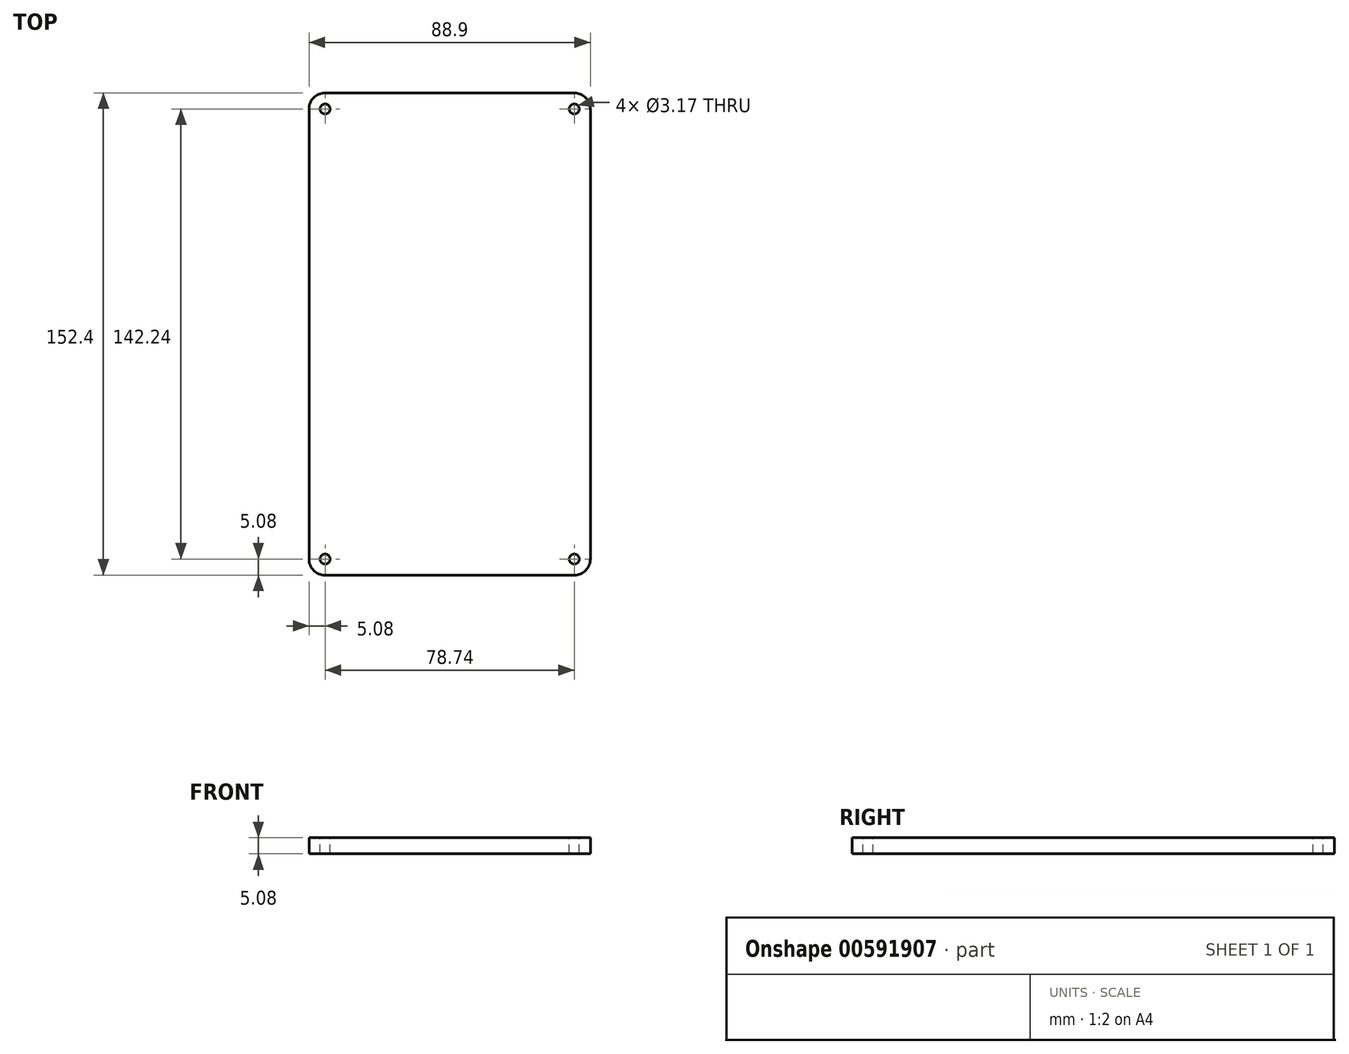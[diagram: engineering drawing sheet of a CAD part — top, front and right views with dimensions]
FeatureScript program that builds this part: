
annotation { "Feature Type Name" : "Feature", "Feature Type Description" : "" }
export const myFeature = defineFeature(function(context is Context, id is Id, definition is map)
    precondition{}
    {
        {
            var Q0;
            Q0=qCreatedBy(makeId("Top.planeOp"),FACE);
            var sketch = newSketch(context, id + "F0", { "sketchPlane" : qUnion([Q0])});
            skLineSegment(sketch, "E0.bottom", {"start": v(0, 0) * mm, "end": v(88.9, 0) * mm});
            skLineSegment(sketch, "E0.top", {"start": v(0, -152.4) * mm, "end": v(88.9, -152.4) * mm});
            skLineSegment(sketch, "E0.left", {"start": v(0, 0) * mm, "end": v(0, -152.4) * mm});
            skLineSegment(sketch, "E0.right", {"start": v(88.9, 0) * mm, "end": v(88.9, -152.4) * mm});
            skSolve(sketch);
        }
        {
            var Q0;
            Q0=makeQuery(id+"F0.imprint","IMPRINT",FACE,{"disambiguationData":[TD([[makeQuery(id+"F0.imprint","IMPRINT",EDGE,{"derivedFrom":sQuery(id+"F0.wireOp",EDGE,"E0.bottom")}),-1.0]])]});
            extrude(context, id + "F1", {"entities" : qUnion([Q0]), "depth" : 5.08 * mm, "offsetDistance" : 25.4 * mm});
        }
        {
            var Q0;
            Q0=makeQuery(id+"F1.opExtrude","CAP_FACE",FACE,{"disambiguationData":[OSD([sQuery(id+"F0.wireOp",EDGE,"E0.bottom"),sQuery(id+"F0.wireOp",EDGE,"E0.top"),sQuery(id+"F0.wireOp",EDGE,"E0.left"),sQuery(id+"F0.wireOp",EDGE,"E0.right")])],"isStart":false});
            var sketch = newSketch(context, id + "F2", { "sketchPlane" : qUnion([Q0])});
            skCircle(sketch, "E1", {"center": v(5.08, -5.08) * mm, "radius": 1.59 * mm});
            skCircle(sketch, "E2", {"center": v(83.82, -5.08) * mm, "radius": 1.59 * mm});
            skCircle(sketch, "E3", {"center": v(5.08, -147.32) * mm, "radius": 1.59 * mm});
            skCircle(sketch, "E4", {"center": v(83.82, -147.32) * mm, "radius": 1.59 * mm});
            skSolve(sketch);
        }
        {
            var Q0;
            Q0=makeQuery(id+"F2.imprint","IMPRINT",FACE,{"disambiguationData":[TD([[makeQuery(id+"F2.imprint","IMPRINT",EDGE,{"derivedFrom":sQuery(id+"F2.wireOp",EDGE,"E1")}),1.0]])]});
            var Q1;
            Q1=makeQuery(id+"F2.imprint","IMPRINT",FACE,{"disambiguationData":[TD([[makeQuery(id+"F2.imprint","IMPRINT",EDGE,{"derivedFrom":sQuery(id+"F2.wireOp",EDGE,"E2")}),1.0]])]});
            var Q2;
            Q2=makeQuery(id+"F2.imprint","IMPRINT",FACE,{"disambiguationData":[TD([[makeQuery(id+"F2.imprint","IMPRINT",EDGE,{"derivedFrom":sQuery(id+"F2.wireOp",EDGE,"E4")}),1.0]])]});
            var Q3;
            Q3=makeQuery(id+"F2.imprint","IMPRINT",FACE,{"disambiguationData":[TD([[makeQuery(id+"F2.imprint","IMPRINT",EDGE,{"derivedFrom":sQuery(id+"F2.wireOp",EDGE,"E3")}),1.0]])]});
            extrude(context, id + "F3", {"entities" : qUnion([Q0, Q1, Q2, Q3]), "operationType" : NewBodyOperationType.REMOVE, "oppositeDirection" : true, "depth" : 25.4 * mm, "offsetDistance" : 25.4 * mm});
        }
        {
            var Q0;
            Q0=makeQuery(id+"F1.opExtrude","SWEPT_EDGE",EDGE,{"disambiguationData":[OSD([sQuery(id+"F0.wireOp",EDGE,"E0.top"),sQuery(id+"F0.wireOp",EDGE,"E0.left")])]});
            var Q1;
            Q1=makeQuery(id+"F1.opExtrude","SWEPT_EDGE",EDGE,{"disambiguationData":[OSD([sQuery(id+"F0.wireOp",EDGE,"E0.top"),sQuery(id+"F0.wireOp",EDGE,"E0.right")])]});
            var Q2;
            Q2=makeQuery(id+"F1.opExtrude","SWEPT_EDGE",EDGE,{"disambiguationData":[OSD([sQuery(id+"F0.wireOp",EDGE,"E0.bottom"),sQuery(id+"F0.wireOp",EDGE,"E0.right")])]});
            var Q3;
            Q3=makeQuery(id+"F1.opExtrude","SWEPT_EDGE",EDGE,{"disambiguationData":[OSD([sQuery(id+"F0.wireOp",EDGE,"E0.bottom"),sQuery(id+"F0.wireOp",EDGE,"E0.left")])]});
            fillet(context, id + "F4", {"entities" : qUnion([Q0, Q1, Q2, Q3]), "tangentPropagation" : true, "radius" : 5.08 * mm, "defaultsChanged" : false, "vertexSettings" : [], "allowEdgeOverflow" : false});
        }
    });
